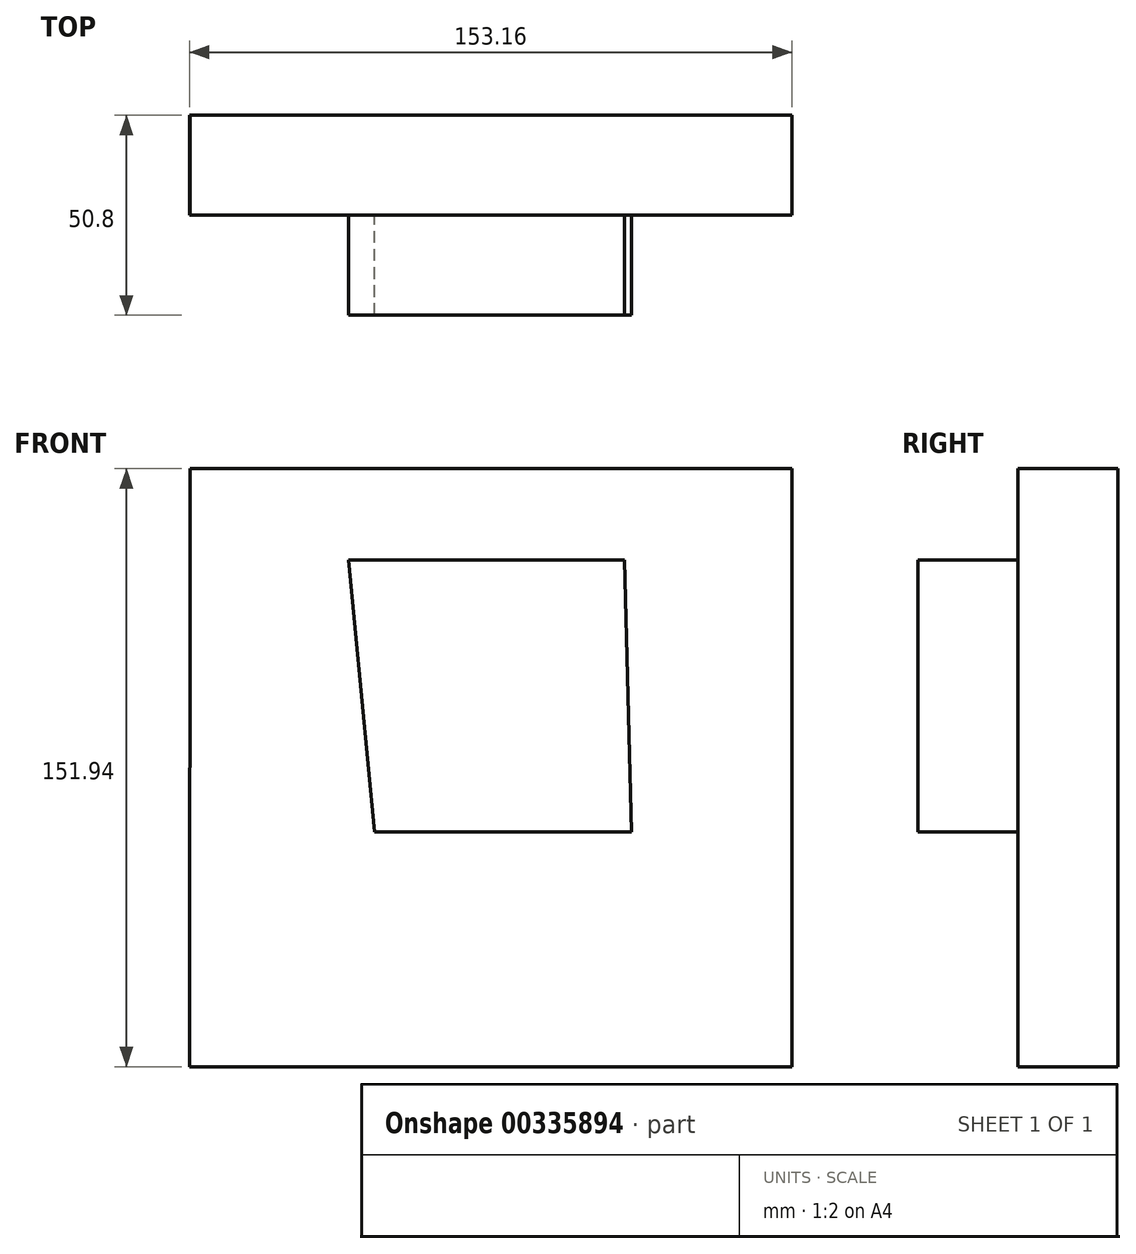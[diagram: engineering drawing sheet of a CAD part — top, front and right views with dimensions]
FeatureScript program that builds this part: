
annotation { "Feature Type Name" : "Feature", "Feature Type Description" : "" }
export const myFeature = defineFeature(function(context is Context, id is Id, definition is map)
    precondition{}
    {
        {
            var Q0;
            Q0=qCreatedBy(makeId("Front.planeOp"),FACE);
            var sketch = newSketch(context, id + "F0", { "sketchPlane" : qUnion([Q0])});
            skLineSegment(sketch, "E0", {"start": v(-76.37, 75.97) * mm, "end": v(76.58, 75.97) * mm});
            skLineSegment(sketch, "E1", {"start": v(76.58, 75.97) * mm, "end": v(76.58, -75.97) * mm});
            skLineSegment(sketch, "E2", {"start": v(76.58, -75.97) * mm, "end": v(-76.58, -75.97) * mm});
            skLineSegment(sketch, "E3", {"start": v(-76.37, 75.97) * mm, "end": v(-76.58, -75.97) * mm});
            skLineSegment(sketch, "E4", {"start": v(-76.37, 75.97) * mm, "end": v(0, 0) * mm});
            skLineSegment(sketch, "E5", {"start": v(76.58, 75.97) * mm, "end": v(0, 0) * mm});
            skLineSegment(sketch, "E6", {"start": v(0, 0) * mm, "end": v(-76.58, -75.97) * mm});
            skLineSegment(sketch, "E7", {"start": v(0, 0) * mm, "end": v(76.58, -75.97) * mm});
            skSolve(sketch);
        }
        {
            var Q0;
            Q0=makeQuery(id+"F0.imprint","IMPRINT",FACE,{"disambiguationData":[TD([[makeQuery(id+"F0.imprint","IMPRINT",EDGE,{"derivedFrom":sQuery(id+"F0.wireOp",EDGE,"E3")}),1.0]])]});
            var Q1;
            Q1=makeQuery(id+"F0.imprint","IMPRINT",FACE,{"disambiguationData":[TD([[makeQuery(id+"F0.imprint","IMPRINT",EDGE,{"derivedFrom":sQuery(id+"F0.wireOp",EDGE,"E0")}),-1.0]])]});
            var Q2;
            Q2=makeQuery(id+"F0.imprint","IMPRINT",FACE,{"disambiguationData":[TD([[makeQuery(id+"F0.imprint","IMPRINT",EDGE,{"derivedFrom":sQuery(id+"F0.wireOp",EDGE,"E1")}),-1.0]])]});
            var Q3;
            Q3=makeQuery(id+"F0.imprint","IMPRINT",FACE,{"disambiguationData":[TD([[makeQuery(id+"F0.imprint","IMPRINT",EDGE,{"derivedFrom":sQuery(id+"F0.wireOp",EDGE,"E2")}),-1.0]])]});
            extrude(context, id + "F1", {"entities" : qUnion([Q0, Q1, Q2, Q3]), "depth" : 25.4 * mm});
        }
        {
            var Q0;
            Q0=makeQuery(id+"F1.opExtrude","CAP_FACE",FACE,{"disambiguationData":[OSD([sQuery(id+"F0.wireOp",EDGE,"E0"),sQuery(id+"F0.wireOp",EDGE,"E1"),sQuery(id+"F0.wireOp",EDGE,"E2"),sQuery(id+"F0.wireOp",EDGE,"E3")])],"isStart":false});
            var sketch = newSketch(context, id + "F2", { "sketchPlane" : qUnion([Q0])});
            skLineSegment(sketch, "E8", {"start": v(-36.17, 52.73) * mm, "end": v(33.94, 52.73) * mm});
            skLineSegment(sketch, "E9", {"start": v(33.94, 52.73) * mm, "end": v(35.76, -16.37) * mm});
            skLineSegment(sketch, "E10", {"start": v(35.76, -16.37) * mm, "end": v(-29.5, -16.37) * mm});
            skLineSegment(sketch, "E11", {"start": v(-36.17, 52.73) * mm, "end": v(-29.5, -16.37) * mm});
            skSolve(sketch);
        }
        {
            var Q0;
            Q0 = qSketchRegion(id + "F2", true);
            extrude(context, id + "F3", {"entities" : qUnion([Q0]), "operationType" : NewBodyOperationType.ADD, "depth" : 25.4 * mm});
        }
    });
